# Revit family: Storage-Mounted-Teknion-JNBDO-Open_Credenza_with_Lateral_File-R2015
name_source: partatom
category: Furniture
revit_build: Autodesk Revit Architecture 2015 (Build: 20140323_1530(x64)
units: mm (PartAtom-declared; Revit-internal decimal feet)

## types (2) — shared parameters
Assembly Code = E2020200
Manufacturer = Teknion
Manufacturer Fax = 416.661.4586
Model = JNBDO
Part Number = JNBDO
Product Documentation Link = http://www.teknion.com
Product Line = Expansion Cityline
Product Page URL = http://www.teknion.com
Series = Expansion Cityline
Sustainability Data = http://www.teknion.com
URL = www.teknion.com
Unit Weight URL = http://www.teknion.com
Warranty = http://www.teknion.com

## per-type parameters (varying)
| type | Description |
| Double-Sided Beam | Semi-Suspended Credenza – Open with Lateral File, Double-Sided |
| Single-Sided Beam | Semi-Suspended Credenza – Open with Lateral File, Single-Sided |

type visibility flags: 2 boolean params named "<type name> Configuration" — each type sets only its own to Yes (folded from table)

## geometry (parser evidence)
native form markers: Sweep x3
no freeform markers — native parametric forms only
